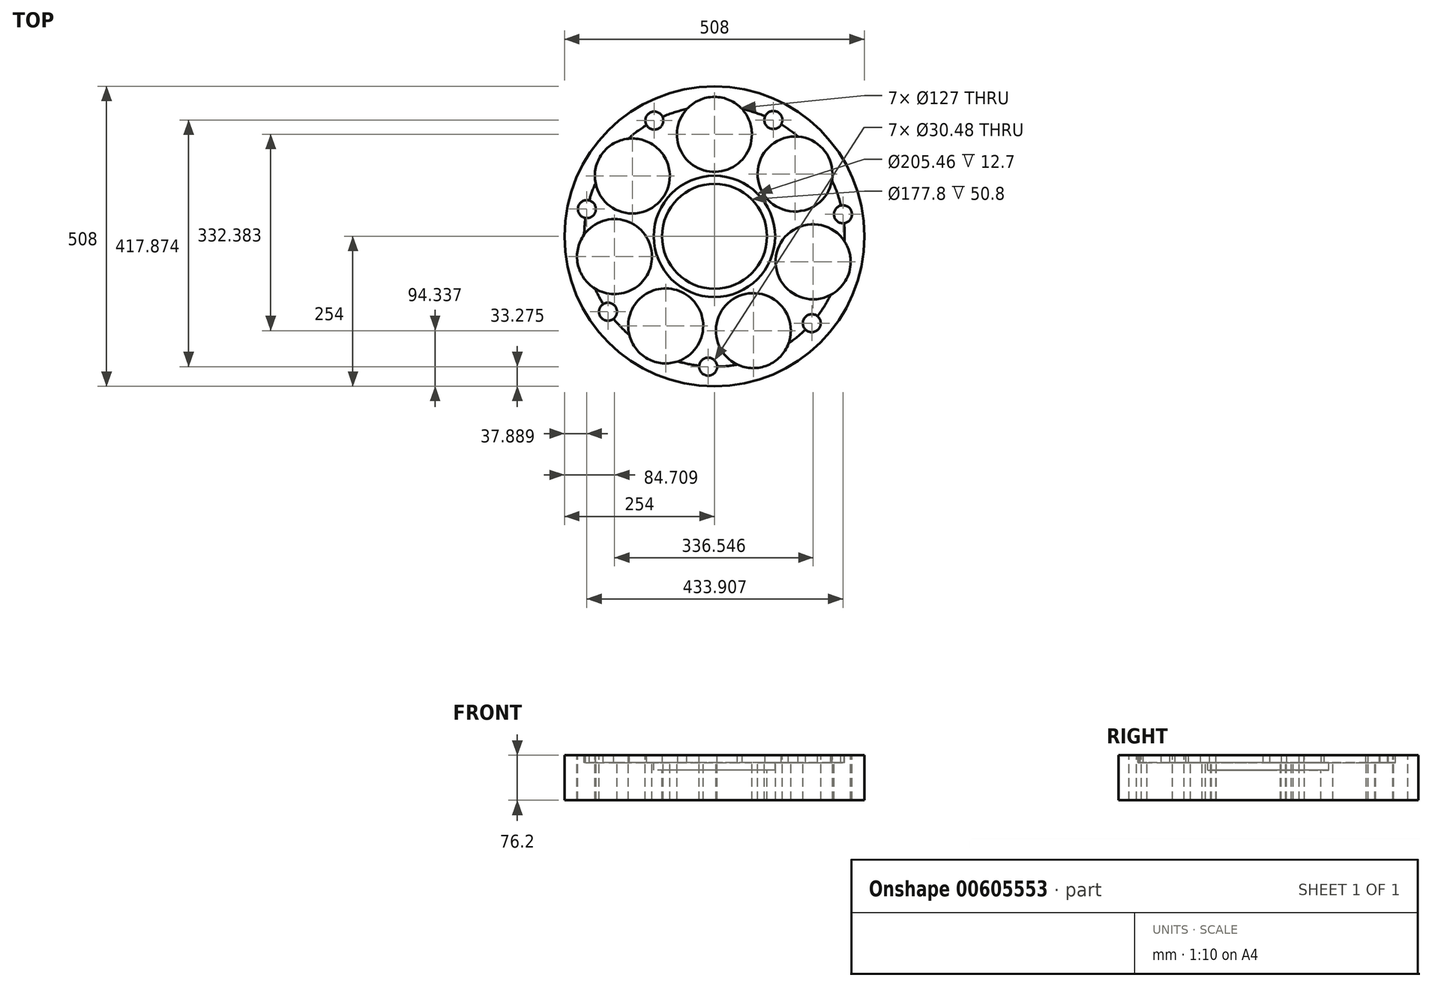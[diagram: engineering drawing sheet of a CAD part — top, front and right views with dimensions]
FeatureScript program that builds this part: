
annotation { "Feature Type Name" : "Feature", "Feature Type Description" : "" }
export const myFeature = defineFeature(function(context is Context, id is Id, definition is map)
    precondition{}
    {
        {
            var Q0;
            Q0=qCreatedBy(makeId("Top.planeOp"),FACE);
            var sketch = newSketch(context, id + "F0", { "sketchPlane" : qUnion([Q0])});
            skCircle(sketch, "E0", {"center": v(0, 0) * mm, "radius": 254 * mm});
            skSolve(sketch);
        }
        {
            var Q0;
            Q0 = qSketchRegion(id + "F0", true);
            extrude(context, id + "F1", {"entities" : qUnion([Q0]), "depth" : 76.2 * mm, "offsetDistance" : 25.4 * mm});
        }
        {
            var Q0;
            Q0=makeQuery(id+"F1.opExtrude","CAP_FACE",FACE,{"disambiguationData":[OSD([sQuery(id+"F0.wireOp",EDGE,"E0")])],"isStart":false});
            var sketch = newSketch(context, id + "F2", { "sketchPlane" : qUnion([Q0])});
            skCircle(sketch, "E1", {"center": v(0, 0) * mm, "radius": 88.9 * mm});
            skSolve(sketch);
        }
        {
            var Q0;
            Q0 = qSketchRegion(id + "F2", true);
            extrude(context, id + "F3", {"entities" : qUnion([Q0]), "operationType" : NewBodyOperationType.REMOVE, "oppositeDirection" : true, "depth" : 152.4 * mm, "offsetDistance" : 25.4 * mm});
        }
        {
            var Q0;
            Q0=makeQuery(id+"F1.opExtrude","CAP_FACE",FACE,{"disambiguationData":[OSD([sQuery(id+"F0.wireOp",EDGE,"E0")])],"isStart":false});
            var sketch = newSketch(context, id + "F4", { "sketchPlane" : qUnion([Q0])});
            skCircle(sketch, "E2", {"center": v(0, 172.72) * mm, "radius": 63.5 * mm});
            skCircle(sketch, "E3", {"center": v(136.62, 105.68) * mm, "radius": 63.5 * mm});
            skCircle(sketch, "E4", {"center": v(167.26, -43.1) * mm, "radius": 63.5 * mm});
            skCircle(sketch, "E5", {"center": v(-82.59, -151.7) * mm, "radius": 63.5 * mm});
            skCircle(sketch, "E6", {"center": v(-169.3, -34.24) * mm, "radius": 63.5 * mm});
            skCircle(sketch, "E7", {"center": v(-139.18, 102.29) * mm, "radius": 63.5 * mm});
            skCircle(sketch, "E8", {"center": v(65.88, -159.66) * mm, "radius": 63.5 * mm});
            skSolve(sketch);
        }
        {
            var Q0;
            Q0 = qSketchRegion(id + "F4", true);
            extrude(context, id + "F5", {"entities" : qUnion([Q0]), "operationType" : NewBodyOperationType.REMOVE, "oppositeDirection" : true, "depth" : 152.4 * mm, "offsetDistance" : 25.4 * mm});
        }
        {
            var Q0;
            Q0=makeQuery(id+"F1.opExtrude","CAP_FACE",FACE,{"disambiguationData":[OSD([sQuery(id+"F0.wireOp",EDGE,"E0")])],"isStart":false});
            var sketch = newSketch(context, id + "F6", { "sketchPlane" : qUnion([Q0])});
            skCircle(sketch, "E9", {"center": v(-101.83, 196.12) * mm, "radius": 15.24 * mm});
            skCircle(sketch, "E10", {"center": v(99.82, 197.15) * mm, "radius": 15.24 * mm});
            skCircle(sketch, "E11", {"center": v(217.8, 37.37) * mm, "radius": 15.24 * mm});
            skCircle(sketch, "E12", {"center": v(164.93, -147.07) * mm, "radius": 15.24 * mm});
            skCircle(sketch, "E13", {"center": v(-180.4, -127.63) * mm, "radius": 15.24 * mm});
            skCircle(sketch, "E14", {"center": v(-216.11, 46.13) * mm, "radius": 15.24 * mm});
            skCircle(sketch, "E15", {"center": v(-10.6, -220.73) * mm, "radius": 15.24 * mm});
            skSolve(sketch);
        }
        {
            var Q0;
            Q0=makeQuery(id+"F6.imprint","IMPRINT",FACE,{"disambiguationData":[TD([[makeQuery(id+"F6.imprint","IMPRINT",EDGE,{"derivedFrom":sQuery(id+"F6.wireOp",EDGE,"E9")}),-1.0]])]});
            var sketch = newSketch(context, id + "F7", { "sketchPlane" : qUnion([Q0])});
            skCircle(sketch, "E16", {"center": v(0, 0) * mm, "radius": 102.73 * mm});
            skSolve(sketch);
        }
        {
            var Q0;
            Q0 = qSketchRegion(id + "F7", true);
            extrude(context, id + "F8", {"entities" : qUnion([Q0]), "operationType" : NewBodyOperationType.REMOVE, "oppositeDirection" : true, "depth" : 25.4 * mm, "offsetDistance" : 25.4 * mm});
        }
        {
            var Q0;
            Q0=makeQuery(id+"F6.imprint","IMPRINT",FACE,{"disambiguationData":[TD([[makeQuery(id+"F6.imprint","IMPRINT",EDGE,{"derivedFrom":sQuery(id+"F6.wireOp",EDGE,"E9")}),-1.0]])]});
            var sketch = newSketch(context, id + "F9", { "sketchPlane" : qUnion([Q0])});
            skCircle(sketch, "E17", {"center": v(0, 0) * mm, "radius": 220.68 * mm});
            skSolve(sketch);
        }
        {
            var Q0;
            Q0 = qSketchRegion(id + "F9", true);
            extrude(context, id + "F10", {"entities" : qUnion([Q0]), "operationType" : NewBodyOperationType.REMOVE, "oppositeDirection" : true, "depth" : 12.7 * mm, "offsetDistance" : 25.4 * mm});
        }
        {
            var Q0;
            Q0 = qSketchRegion(id + "F6", true);
            extrude(context, id + "F11", {"entities" : qUnion([Q0]), "operationType" : NewBodyOperationType.REMOVE, "oppositeDirection" : true, "depth" : 152.4 * mm, "offsetDistance" : 25.4 * mm});
        }
    });
